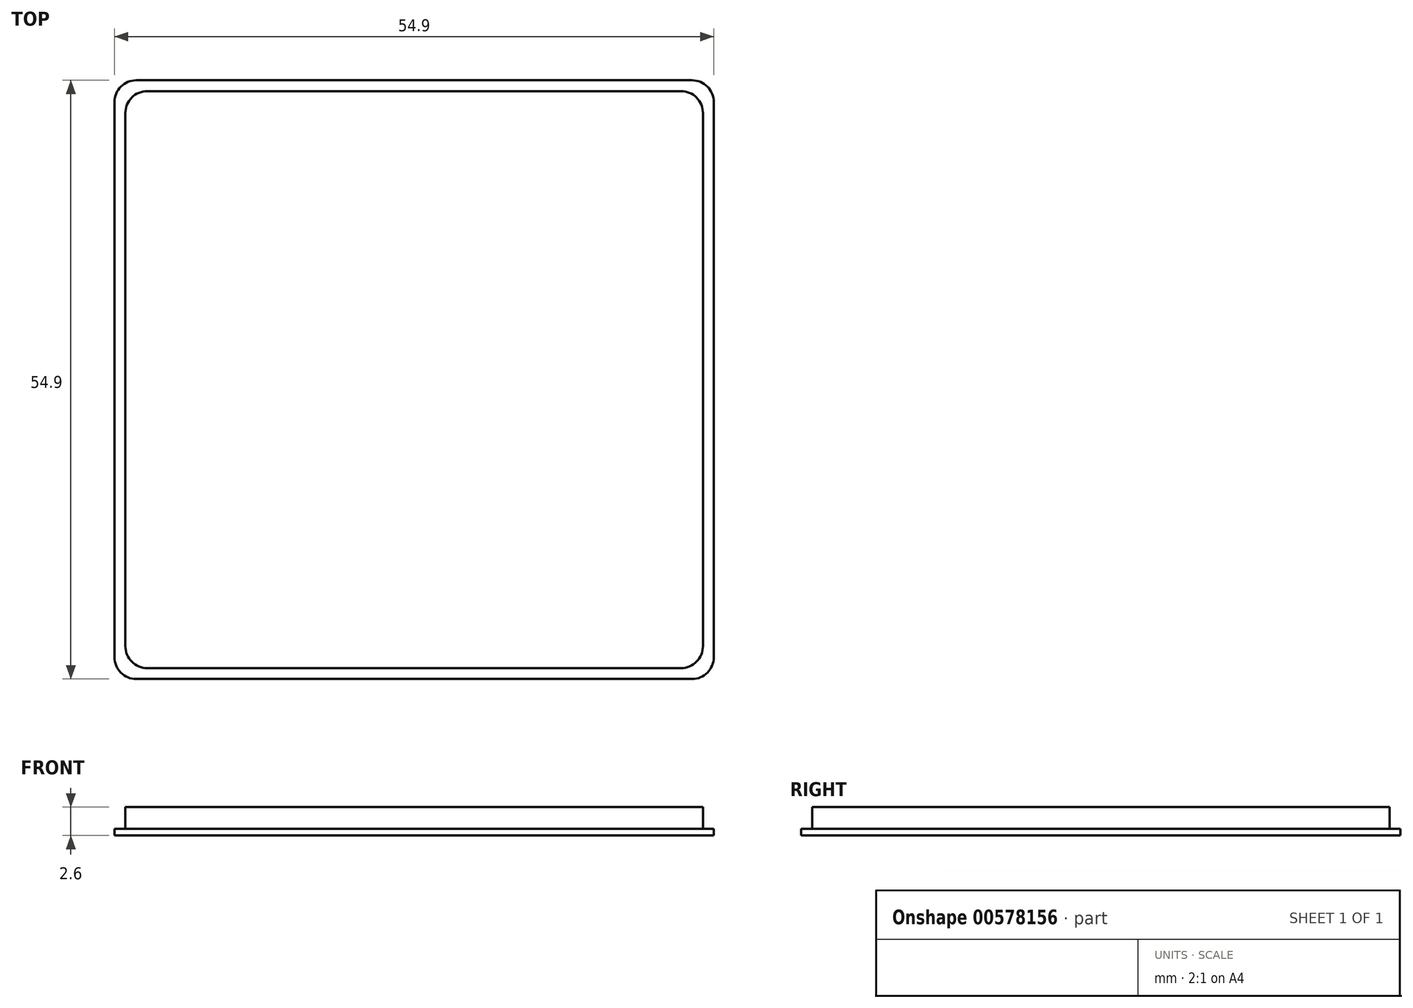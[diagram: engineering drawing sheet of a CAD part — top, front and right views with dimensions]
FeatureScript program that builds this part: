
annotation { "Feature Type Name" : "Feature", "Feature Type Description" : "" }
export const myFeature = defineFeature(function(context is Context, id is Id, definition is map)
    precondition{}
    {
        {
            var Q0;
            Q0=qCreatedBy(makeId("Top.planeOp"),FACE);
            var sketch = newSketch(context, id + "F0", { "sketchPlane" : qUnion([Q0])});
            skPoint(sketch, "E0.middle", {"position": v(0, 0) * mm});
            skLineSegment(sketch, "E1.bottom", {"start": v(-27.45, -27.45) * mm, "end": v(27.45, -27.45) * mm});
            skLineSegment(sketch, "E1.top", {"start": v(-27.45, 27.45) * mm, "end": v(27.45, 27.45) * mm});
            skLineSegment(sketch, "E1.left", {"start": v(-27.45, -27.45) * mm, "end": v(-27.45, 27.45) * mm});
            skLineSegment(sketch, "E1.right", {"start": v(27.45, -27.45) * mm, "end": v(27.45, 27.45) * mm});
            skLineSegment(sketch, "E2.bottom", {"start": v(26.45, -26.45) * mm, "end": v(-26.45, -26.45) * mm});
            skLineSegment(sketch, "E2.top", {"start": v(26.45, 26.45) * mm, "end": v(-26.45, 26.45) * mm});
            skLineSegment(sketch, "E2.left", {"start": v(26.45, -26.45) * mm, "end": v(26.45, 26.45) * mm});
            skLineSegment(sketch, "E2.right", {"start": v(-26.45, -26.45) * mm, "end": v(-26.45, 26.45) * mm});
            skSolve(sketch);
        }
        {
            var Q0;
            Q0=makeQuery(id+"F0.imprint","IMPRINT",FACE,{"disambiguationData":[TD([[makeQuery(id+"F0.imprint","IMPRINT",EDGE,{"derivedFrom":sQuery(id+"F0.wireOp",EDGE,"E2.bottom")}),-1.0]])]});
            extrude(context, id + "F1", {"entities" : qUnion([Q0]), "depth" : 2.6 * mm, "offsetDistance" : 25 * mm});
        }
        {
            var Q0;
            Q0=makeQuery(id+"F0.imprint","IMPRINT",FACE,{"disambiguationData":[TD([[makeQuery(id+"F0.imprint","IMPRINT",EDGE,{"derivedFrom":sQuery(id+"F0.wireOp",EDGE,"E1.bottom")}),1.0]])]});
            extrude(context, id + "F2", {"entities" : qUnion([Q0]), "operationType" : NewBodyOperationType.ADD, "depth" : 0.6 * mm, "offsetDistance" : 25 * mm});
        }
        {
            var Q0;
            Q0=makeQuery(id+"F1.opExtrude","SWEPT_EDGE",EDGE,{"disambiguationData":[OSD([sQuery(id+"F0.wireOp",EDGE,"E2.bottom"),sQuery(id+"F0.wireOp",EDGE,"E2.right")])]});
            var Q1;
            Q1=makeQuery(id+"F1.opExtrude","SWEPT_EDGE",EDGE,{"disambiguationData":[OSD([sQuery(id+"F0.wireOp",EDGE,"E2.bottom"),sQuery(id+"F0.wireOp",EDGE,"E2.left")])]});
            var Q2;
            Q2=makeQuery(id+"F1.opExtrude","SWEPT_EDGE",EDGE,{"disambiguationData":[OSD([sQuery(id+"F0.wireOp",EDGE,"E2.top"),sQuery(id+"F0.wireOp",EDGE,"E2.right")])]});
            var Q3;
            Q3=makeQuery(id+"F1.opExtrude","SWEPT_EDGE",EDGE,{"disambiguationData":[OSD([sQuery(id+"F0.wireOp",EDGE,"E2.top"),sQuery(id+"F0.wireOp",EDGE,"E2.left")])]});
            var Q4;
            Q4=makeQuery(id+"F2.opExtrude","SWEPT_EDGE",EDGE,{"disambiguationData":[OSD([sQuery(id+"F0.wireOp",EDGE,"E1.top"),sQuery(id+"F0.wireOp",EDGE,"E1.left")])]});
            var Q5;
            Q5=makeQuery(id+"F2.opExtrude","SWEPT_EDGE",EDGE,{"disambiguationData":[OSD([sQuery(id+"F0.wireOp",EDGE,"E1.bottom"),sQuery(id+"F0.wireOp",EDGE,"E1.left")])]});
            var Q6;
            Q6=makeQuery(id+"F2.opExtrude","SWEPT_EDGE",EDGE,{"disambiguationData":[OSD([sQuery(id+"F0.wireOp",EDGE,"E1.bottom"),sQuery(id+"F0.wireOp",EDGE,"E1.right")])]});
            var Q7;
            Q7=makeQuery(id+"F2.opExtrude","SWEPT_EDGE",EDGE,{"disambiguationData":[OSD([sQuery(id+"F0.wireOp",EDGE,"E1.top"),sQuery(id+"F0.wireOp",EDGE,"E1.right")])]});
            fillet(context, id + "F3", {"entities" : qUnion([Q0, Q1, Q2, Q3, Q4, Q5, Q6, Q7]), "radius" : 2 * mm, "tangentPropagation" : true, "allowEdgeOverflow" : false});
        }
    });
